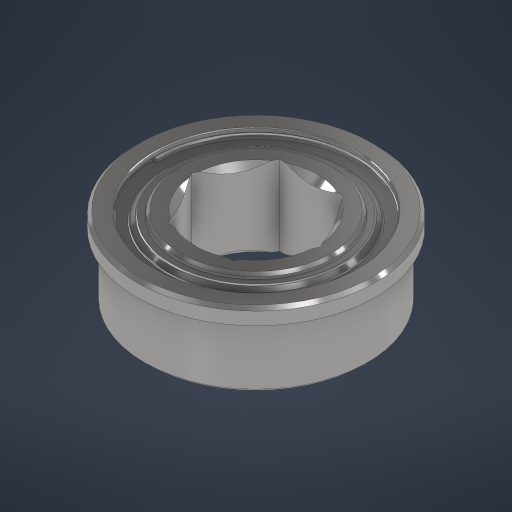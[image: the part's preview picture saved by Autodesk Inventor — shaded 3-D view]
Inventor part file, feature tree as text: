
AUTODESK INVENTOR PART (.ipt)
format: ipt  version: 2024 (Build 280153000, 153)  size: 372,736 bytes
history: native  units: in
note: dims shown in document units (in); Inventor stores cm internally (conversion verified against a paired STEP export)
features: mirror x2, revolve x1
ambient origin geometry x8: Origin, YZ Plane, XZ Plane, XY Plane, X Axis, Y Axis, Z Axis, Center Point
bodies: Solid1 (feature_tree), Solid2 (feature_tree), Solid3 (feature_tree)
feature tree (3):
  revolve  "Revolve1"  [1 undecoded]
  mirror  "Mirror3"
  mirror  "Mirror5"
note: 1 required parameter value undecoded (feature->parameter linkage not recoverable at this tier; creation-order binding heuristic only, values carry confidence <= 0.55)
